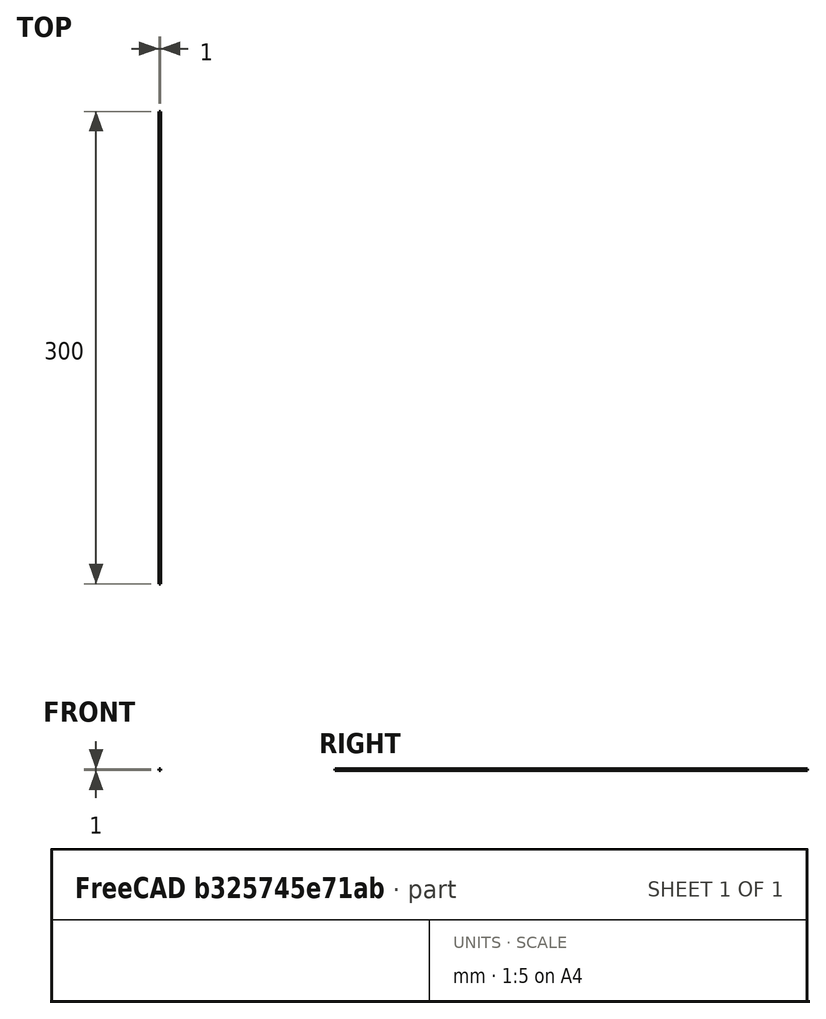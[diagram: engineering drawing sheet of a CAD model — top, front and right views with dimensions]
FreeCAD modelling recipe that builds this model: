
FCSTD DOCUMENT  (FreeCAD 0.18R16110 (Git))
Label: пруток
License: All rights reserved
LicenseURL: http://en.wikipedia.org/wiki/All_rights_reserved
objects: Sketcher::SketchObject×1, PartDesign::Pad×1, PartDesign::Body×1
note: 4 computed .brp shape members not serialized (recipe doc carries the construction recipe); baked Part::Feature solids carry a one-line shape summary decoded from their .brp

FEATURE [Sketcher::SketchObject] Sketch
  MapMode = 5
  Placement = pos=(0,0,0) rot=(1,0,0;1.5708rad)
  Support = -> [XZ_Plane]
  sketch-geometry (4):
    g0: LineSegment StartX=0 StartY=0 StartZ=0 EndX=1 EndY=0 EndZ=0
    g1: LineSegment StartX=1 StartY=0 StartZ=0 EndX=1 EndY=1 EndZ=0
    g2: LineSegment StartX=1 StartY=1 StartZ=0 EndX=0 EndY=1 EndZ=0
    g3: LineSegment StartX=0 StartY=1 StartZ=0 EndX=0 EndY=0 EndZ=0
  constraints (11):
    c: Coincident(g0,g1)
    c: Coincident(g1,g2)
    c: Coincident(g2,g3)
    c: Coincident(g3,g0)
    c: Horizontal(g0)
    c: Horizontal(g2)
    c: Vertical(g1)
    c: Vertical(g3)
    c: DistanceX(g2,g2) = 1
    c: DistanceY(g1,g1) = 1
    c: Coincident(g0,g-1)
FEATURE [PartDesign::Pad] Pad
  Length = 300
  Length2 = 100
  Placement = pos=(0,0,0) rot=(1,0,0;1.5708rad)
  Profile = -> Sketch
  Type = 0
FEATURE [PartDesign::Body] Body
  Group = -> [Sketch,Pad]
  Origin = -> Origin
  Tip = -> Pad
